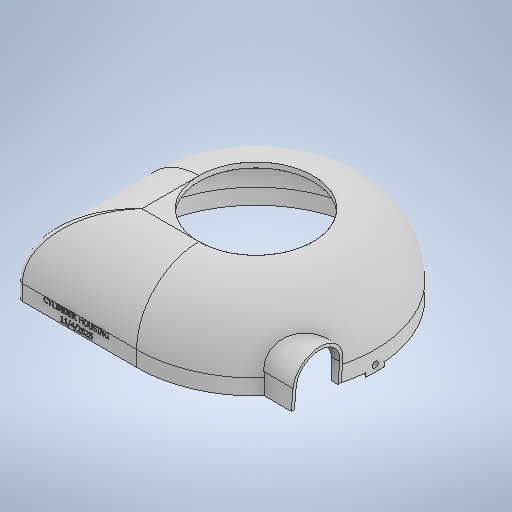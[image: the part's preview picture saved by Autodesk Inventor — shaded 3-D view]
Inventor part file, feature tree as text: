
AUTODESK INVENTOR PART (.ipt)
format: ipt  version: 2025 (Build 290162000, 162)  size: 903,680 bytes
history: native  units: mm
features: sketch x9, extrude x7, fillet x2, projected_geometry x2, hole x1, plane x1, emboss x1
ambient origin geometry x8: Origin, YZ Plane, XZ Plane, XY Plane, X Axis, Y Axis, Z Axis, Center Point
bodies: Solid1 (feature_tree)
feature tree (23):
  extrude  "Base Shape & Wall"  Depth=5.0mm
  fillet  "Curved Edge"  Radius=75.0mm
  hole  "Cylinder Hole"  [1 undecoded]
  extrude  "Front Tab"  Depth=5.9mm
  extrude  "Bolt Hole"  Depth=4.0mm TaperAngle=0.0deg
  extrude  "Hinge Tab Recess"  Depth=6.5mm
  extrude  "LV Hole"  Depth=15.0mm TaperAngle=0.0deg
  plane  "Work Plane1"
  extrude  "LV Hood"  Depth=53.226mm
  extrude  "Hood Slant Cut"  TaperAngle=0.0deg  [1 undecoded]
  fillet  "Fillet2"  Radius=115.0mm
  emboss  "Emboss1"
  sketch  "Sketch1"  dims[d0=230.0mm d1=5.0mm d2=75.0mm d3=0.0mm]
  sketch  "Sketch2"  dims[d4=60.0mm d5=4.9mm]
  sketch  "Sketch3"  dims[d6=109.9mm d7=6.0mm d8=4.0mm d9=2.0mm d10=90.0deg d11=8.0mm d12=20.594885mm d13=5.9mm]
  projected_geometry  "Projected Loop1"
  sketch  "Sketch4"  dims[d14=8.9mm d15=4.0mm d16=0.0mm]
  sketch  "Sketch5"  dims[d17=5.5mm d18=6.5mm]
  sketch  "Sketch6"  dims[d19=0.0mm d20=0.0mm d23=15.0mm d24=0.0mm]
  sketch  "Sketch8"  dims[d25=42.0mm d26=53.226mm]
  sketch  "Sketch9"  dims[d27=20.0mm d28=0.0mm d29=0.0mm d30=115.0mm]
  projected_geometry  "Projected Loop2"
  sketch  "Sketch10"  dims[d38=3.0mm d39=10.0mm d40=0.0mm d41=10.0mm d42=0.0mm d43=10.1mm d44=3.0mm d45=0.2mm d46=1.0mm d47=0.0mm d34=0.5mm d35=0.872665mm d36=0.5mm d37=0.872665mm]
note: 2 required parameter values undecoded (feature->parameter linkage not recoverable at this tier; creation-order binding heuristic only, values carry confidence <= 0.55)
